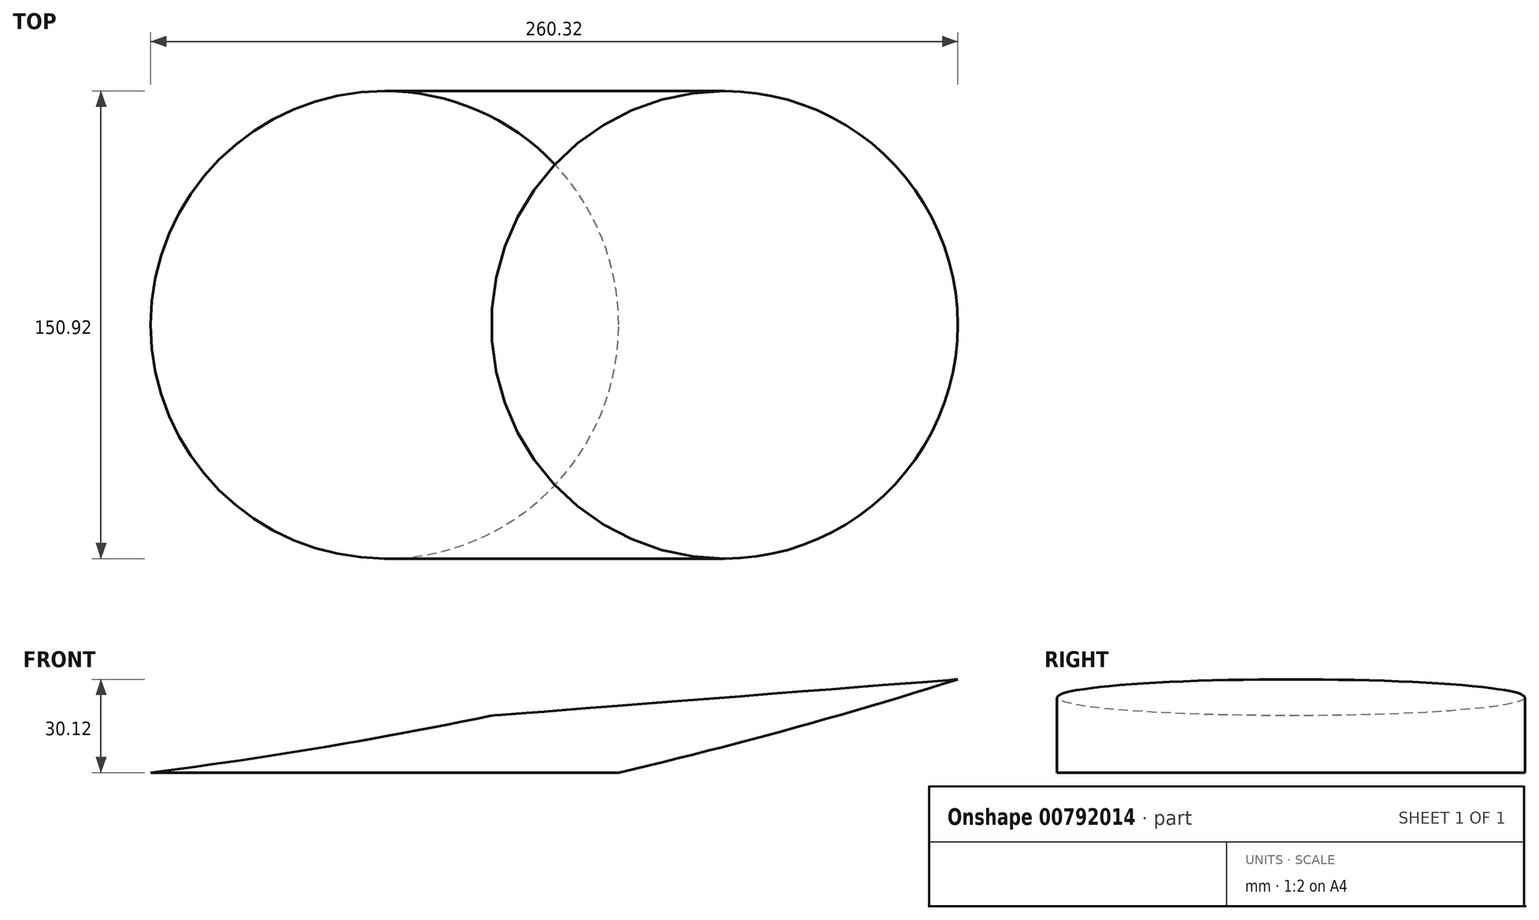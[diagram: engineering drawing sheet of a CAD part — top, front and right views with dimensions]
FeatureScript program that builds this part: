
annotation { "Feature Type Name" : "Feature", "Feature Type Description" : "" }
export const myFeature = defineFeature(function(context is Context, id is Id, definition is map)
    precondition{}
    {
        {
            var Q0;
            Q0=qCreatedBy(makeId("Top.planeOp"),FACE);
            var sketch = newSketch(context, id + "F0", { "sketchPlane" : qUnion([Q0])});
            skCircle(sketch, "E0", {"center": v(0, 0) * mm, "radius": 75.46 * mm});
            skSolve(sketch);
        }
        {
            var Q0;
            Q0=qCreatedBy(makeId("Front.planeOp"),FACE);
            var sketch = newSketch(context, id + "F1", { "sketchPlane" : qUnion([Q0])});
            skArc(sketch, "E1", {"start": v(0, 0) * mm, "mid": v(55.05, 11.06) * mm, "end": v(109.62, 24.26) * mm});
            skArc(sketch, "E2", {"start": v(173.17, 81.3) * mm, "mid": v(109.92, 87.85) * mm, "end": v(109.62, 24.26) * mm});
            skSolve(sketch);
        }
        {
            var Q0;
            Q0=makeQuery(id+"F0.imprint","IMPRINT",FACE,{"disambiguationData":[TD([[makeQuery(id+"F0.imprint","IMPRINT",EDGE,{"derivedFrom":sQuery(id+"F0.wireOp",EDGE,"E0")}),1.0]])]});
            var Q1;
            Q1=sQuery(id+"F1.wireOp",EDGE,"E1");
            sweep(context, id + "F2", {"profiles" : qUnion([Q0]), "path" : qUnion([Q1])});
        }
    });
